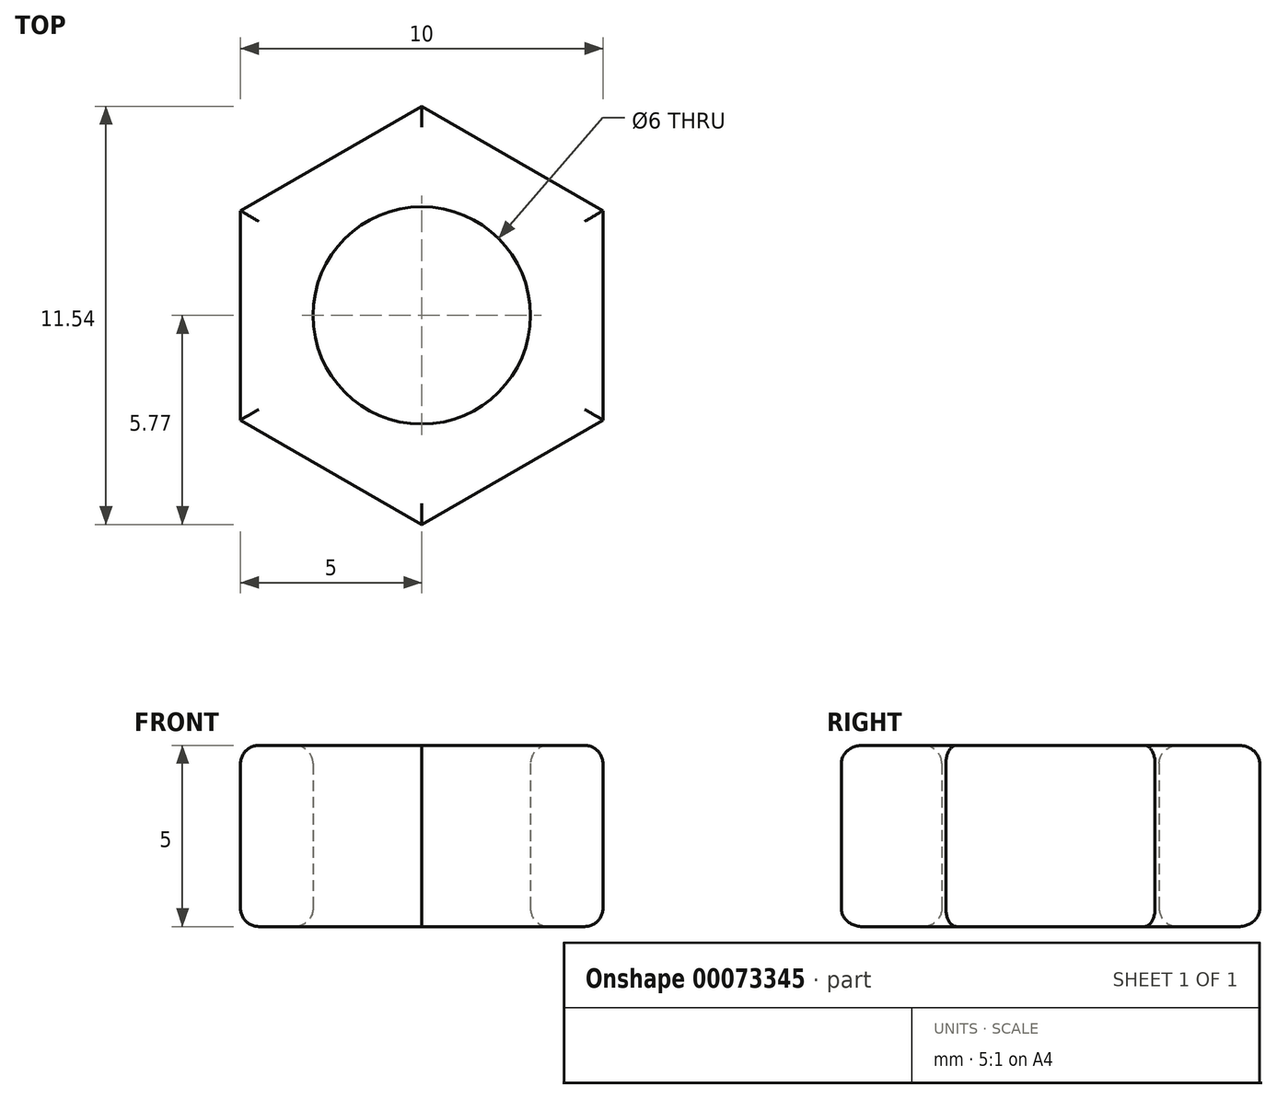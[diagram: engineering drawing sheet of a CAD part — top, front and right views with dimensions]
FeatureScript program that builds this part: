
annotation { "Feature Type Name" : "Feature", "Feature Type Description" : "" }
export const myFeature = defineFeature(function(context is Context, id is Id, definition is map)
    precondition{}
    {
        {
            var Q0;
            Q0=qCreatedBy(makeId("Top.planeOp"),FACE);
            var sketch = newSketch(context, id + "F0", { "sketchPlane" : qUnion([Q0])});
            skCircle(sketch, "E0", {"center": v(0, 0) * mm, "radius": 5.77 * mm});
            skPoint(sketch, "E1", {"position": v(0, 5.77) * mm});
            skPoint(sketch, "E2.1.0", {"position": v(-5, 2.89) * mm});
            skPoint(sketch, "E2.2.0", {"position": v(-5, -2.89) * mm});
            skPoint(sketch, "E2.3.0", {"position": v(0, -5.77) * mm});
            skPoint(sketch, "E2.4.0", {"position": v(5, -2.89) * mm});
            skPoint(sketch, "E2.5.0", {"position": v(5, 2.89) * mm});
            skLineSegment(sketch, "E3", {"start": v(0, 5.77) * mm, "end": v(5, 2.89) * mm});
            skLineSegment(sketch, "E4", {"start": v(5, 2.89) * mm, "end": v(5, -2.89) * mm});
            skLineSegment(sketch, "E5", {"start": v(5, -2.89) * mm, "end": v(0, -5.77) * mm});
            skLineSegment(sketch, "E6", {"start": v(0, -5.77) * mm, "end": v(-5, -2.89) * mm});
            skLineSegment(sketch, "E7", {"start": v(-5, -2.89) * mm, "end": v(-5, 2.89) * mm});
            skLineSegment(sketch, "E8", {"start": v(-5, 2.89) * mm, "end": v(0, 5.77) * mm});
            skCircle(sketch, "E9", {"center": v(0, 0) * mm, "radius": 3 * mm});
            skSolve(sketch);
        }
        {
            var Q0;
            Q0=makeQuery(id+"F0.imprint","IMPRINT",FACE,{"disambiguationData":[TD([[makeQuery(id+"F0.imprint","IMPRINT",EDGE,{"derivedFrom":sQuery(id+"F0.wireOp",EDGE,"E3")}),-1.0]])]});
            extrude(context, id + "F1", {"entities" : qUnion([Q0]), "depth" : 5 * mm, "offsetDistance" : 25 * mm});
        }
        {
            var Q0;
            Q0=makeQuery(id+"F1.opExtrude","CAP_EDGE",EDGE,{"disambiguationData":[OSD([sQuery(id+"F0.wireOp",EDGE,"E9")])],"isStart":false});
            var Q1;
            Q1=makeQuery(id+"F1.opExtrude","CAP_EDGE",EDGE,{"disambiguationData":[OSD([sQuery(id+"F0.wireOp",EDGE,"E9")])],"isStart":true});
            var Q2;
            Q2=makeQuery(id+"F1.opExtrude","CAP_EDGE",EDGE,{"disambiguationData":[OSD([sQuery(id+"F0.wireOp",EDGE,"E5")])],"isStart":true});
            var Q3;
            Q3=makeQuery(id+"F1.opExtrude","CAP_EDGE",EDGE,{"disambiguationData":[OSD([sQuery(id+"F0.wireOp",EDGE,"E6")])],"isStart":true});
            var Q4;
            Q4=makeQuery(id+"F1.opExtrude","CAP_EDGE",EDGE,{"disambiguationData":[OSD([sQuery(id+"F0.wireOp",EDGE,"E6")])],"isStart":false});
            var Q5;
            Q5=makeQuery(id+"F1.opExtrude","CAP_EDGE",EDGE,{"disambiguationData":[OSD([sQuery(id+"F0.wireOp",EDGE,"E5")])],"isStart":false});
            var Q6;
            Q6=makeQuery(id+"F1.opExtrude","CAP_EDGE",EDGE,{"disambiguationData":[OSD([sQuery(id+"F0.wireOp",EDGE,"E4")])],"isStart":false});
            var Q7;
            Q7=makeQuery(id+"F1.opExtrude","CAP_EDGE",EDGE,{"disambiguationData":[OSD([sQuery(id+"F0.wireOp",EDGE,"E3")])],"isStart":false});
            var Q8;
            Q8=makeQuery(id+"F1.opExtrude","CAP_EDGE",EDGE,{"disambiguationData":[OSD([sQuery(id+"F0.wireOp",EDGE,"E8")])],"isStart":false});
            var Q9;
            Q9=makeQuery(id+"F1.opExtrude","CAP_EDGE",EDGE,{"disambiguationData":[OSD([sQuery(id+"F0.wireOp",EDGE,"E7")])],"isStart":false});
            var Q10;
            Q10=makeQuery(id+"F1.opExtrude","CAP_EDGE",EDGE,{"disambiguationData":[OSD([sQuery(id+"F0.wireOp",EDGE,"E4")])],"isStart":true});
            var Q11;
            Q11=makeQuery(id+"F1.opExtrude","CAP_EDGE",EDGE,{"disambiguationData":[OSD([sQuery(id+"F0.wireOp",EDGE,"E3")])],"isStart":true});
            var Q12;
            Q12=makeQuery(id+"F1.opExtrude","CAP_EDGE",EDGE,{"disambiguationData":[OSD([sQuery(id+"F0.wireOp",EDGE,"E8")])],"isStart":true});
            var Q13;
            Q13=makeQuery(id+"F1.opExtrude","CAP_EDGE",EDGE,{"disambiguationData":[OSD([sQuery(id+"F0.wireOp",EDGE,"E7")])],"isStart":true});
            fillet(context, id + "F2", {"entities" : qUnion([Q0, Q1, Q2, Q3, Q4, Q5, Q6, Q7, Q8, Q9, Q10, Q11, Q12, Q13]), "radius" : 0.5 * mm, "tangentPropagation" : true, "allowEdgeOverflow" : false});
        }
    });
